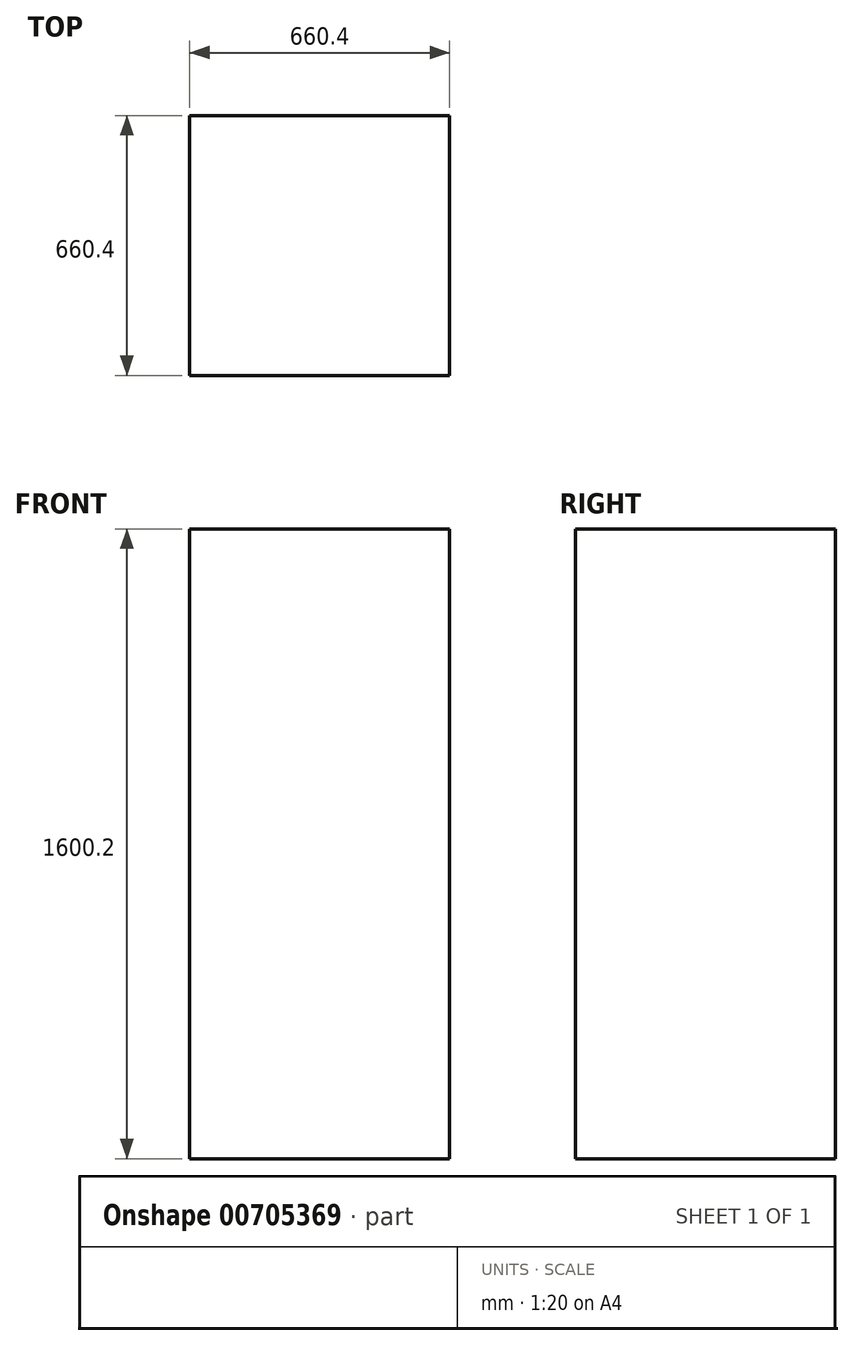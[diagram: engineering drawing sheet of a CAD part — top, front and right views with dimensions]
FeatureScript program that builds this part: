
annotation { "Feature Type Name" : "Feature", "Feature Type Description" : "" }
export const myFeature = defineFeature(function(context is Context, id is Id, definition is map)
    precondition{}
    {
        {
            var Q0;
            Q0=qCreatedBy(makeId("Top.planeOp"),FACE);
            var sketch = newSketch(context, id + "F0", { "sketchPlane" : qUnion([Q0])});
            skLineSegment(sketch, "E0.bottom", {"start": v(0, 0) * mm, "end": v(660.4, 0) * mm});
            skLineSegment(sketch, "E0.top", {"start": v(0, 660.4) * mm, "end": v(660.4, 660.4) * mm});
            skLineSegment(sketch, "E0.left", {"start": v(0, 0) * mm, "end": v(0, 660.4) * mm});
            skLineSegment(sketch, "E0.right", {"start": v(660.4, 0) * mm, "end": v(660.4, 660.4) * mm});
            skSolve(sketch);
        }
        {
            var Q0;
            Q0=makeQuery(id+"F0.imprint","IMPRINT",FACE,{"disambiguationData":[TD([[makeQuery(id+"F0.imprint","IMPRINT",EDGE,{"derivedFrom":sQuery(id+"F0.wireOp",EDGE,"E0.bottom")}),1.0]])]});
            extrude(context, id + "F1", {"entities" : qUnion([Q0]), "depth" : 1600.2 * mm, "offsetDistance" : 25.4 * mm});
        }
    });
